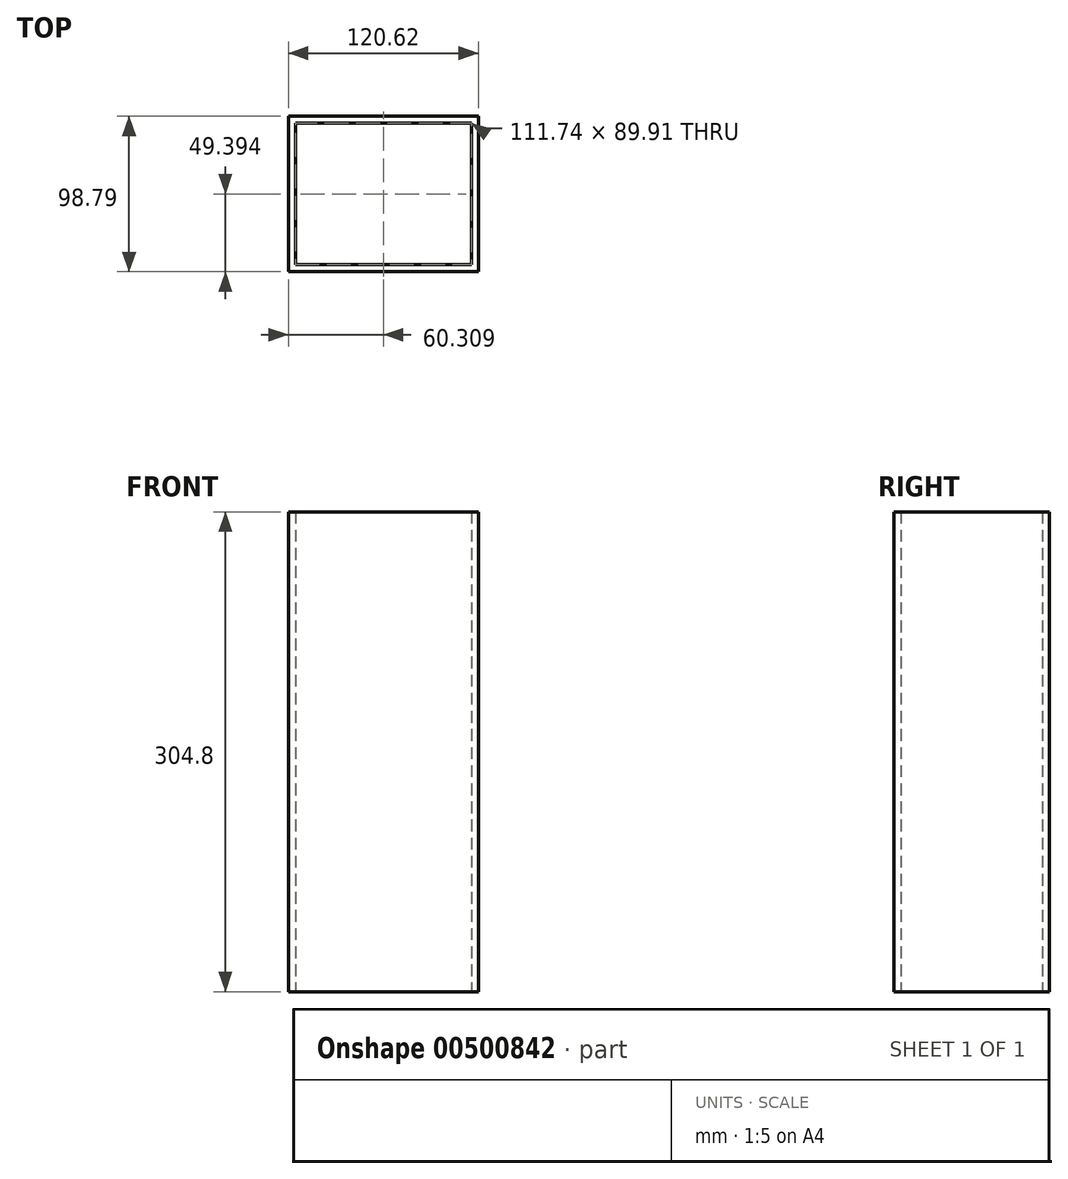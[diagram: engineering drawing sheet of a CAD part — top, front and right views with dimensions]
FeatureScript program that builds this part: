
annotation { "Feature Type Name" : "Feature", "Feature Type Description" : "" }
export const myFeature = defineFeature(function(context is Context, id is Id, definition is map)
    precondition{}
    {
        {
            var Q0;
            Q0=qCreatedBy(makeId("Top.planeOp"),FACE);
            var sketch = newSketch(context, id + "F0", { "sketchPlane" : qUnion([Q0])});
            skLineSegment(sketch, "E0.bottom", {"start": v(-64.59, 60.92) * mm, "end": v(56.03, 60.92) * mm});
            skLineSegment(sketch, "E0.top", {"start": v(-64.59, -37.87) * mm, "end": v(56.03, -37.87) * mm});
            skLineSegment(sketch, "E0.left", {"start": v(-64.59, 60.92) * mm, "end": v(-64.59, -37.87) * mm});
            skLineSegment(sketch, "E0.right", {"start": v(56.03, 60.92) * mm, "end": v(56.03, -37.87) * mm});
            skLineSegment(sketch, "E1.0", {"start": v(-60.15, 56.48) * mm, "end": v(-60.15, -33.43) * mm});
            skLineSegment(sketch, "E1.1", {"start": v(-60.15, 56.48) * mm, "end": v(51.59, 56.48) * mm});
            skLineSegment(sketch, "E1.2", {"start": v(51.59, 56.48) * mm, "end": v(51.59, -33.43) * mm});
            skLineSegment(sketch, "E1.3", {"start": v(-60.15, -33.43) * mm, "end": v(51.59, -33.43) * mm});
            skSolve(sketch);
        }
        {
            var Q0;
            Q0 = qSketchRegion(id + "F0", true);
            extrude(context, id + "F1", {"entities" : qUnion([Q0]), "depth" : 304.8 * mm});
        }
    });
